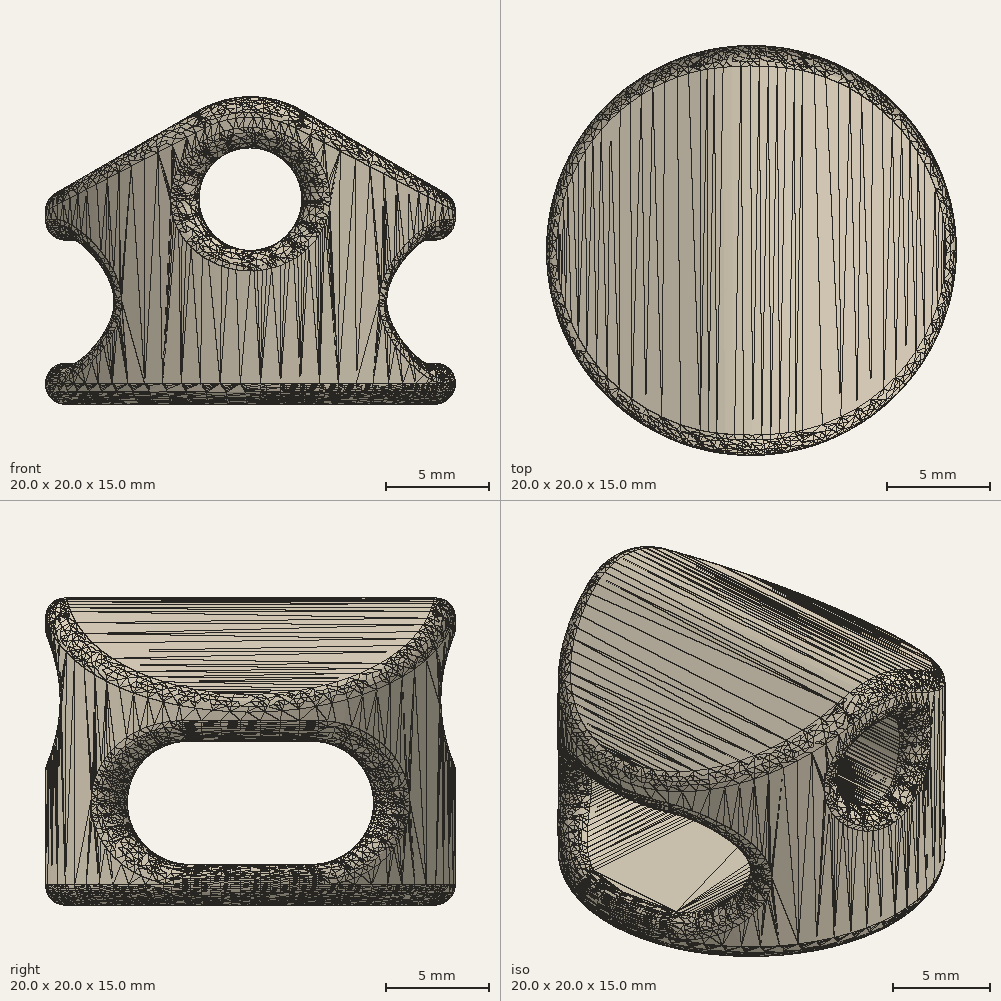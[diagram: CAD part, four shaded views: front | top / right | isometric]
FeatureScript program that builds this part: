
annotation { "Feature Type Name" : "Feature", "Feature Type Description" : "" }
export const myFeature = defineFeature(function(context is Context, id is Id, definition is map)
    precondition{}
    {
        {
            var Q0;
            Q0=qCreatedBy(makeId("Top.planeOp"),FACE);
            var sketch = newSketch(context, id + "F0", { "sketchPlane" : qUnion([Q0])});
            skCircle(sketch, "E0", {"center": v(0, 0) * mm, "radius": 10 * mm});
            skSolve(sketch);
        }
        {
            var Q0;
            Q0 = qSketchRegion(id + "F0", true);
            extrude(context, id + "F1", {"entities" : qUnion([Q0]), "depth" : 10 * mm, "offsetDistance" : 25 * mm, "hasSecondDirection" : true, "secondDirectionOppositeDirection" : true, "secondDirectionDepth" : 5 * mm});
        }
        {
            var Q0;
            Q0=qCreatedBy(makeId("Right.planeOp"),FACE);
            var sketch = newSketch(context, id + "F2", { "sketchPlane" : qUnion([Q0])});
            skLineSegment(sketch, "E1", {"start": v(-3, 0) * mm, "end": v(3, 0) * mm});
            skPoint(sketch, "E2", {"position": v(0, 0) * mm});
            skArc(sketch, "E3.0.startCap", {"start": v(-3, -3) * mm, "mid": v(-6, 0) * mm, "end": v(-3, 3) * mm});
            skArc(sketch, "E3.0.endCap", {"start": v(3, 3) * mm, "mid": v(6, 0) * mm, "end": v(3, -3) * mm});
            skLineSegment(sketch, "E3.0.left", {"start": v(-3, 3) * mm, "end": v(3, 3) * mm});
            skLineSegment(sketch, "E3.0.right", {"start": v(-3, -3) * mm, "end": v(3, -3) * mm});
            skSolve(sketch);
        }
        {
            var Q0;
            Q0 = qSketchRegion(id + "F2", true);
            extrude(context, id + "F3", {"entities" : qUnion([Q0]), "operationType" : NewBodyOperationType.REMOVE, "oppositeDirection" : true, "depth" : 25 * mm, "offsetDistance" : 25 * mm, "hasSecondDirection" : true, "secondDirectionOppositeDirection" : false, "secondDirectionDepth" : 25 * mm});
        }
        {
            var Q0;
            Q0=qCreatedBy(makeId("Front.planeOp"),FACE);
            var sketch = newSketch(context, id + "F4", { "sketchPlane" : qUnion([Q0])});
            skCircle(sketch, "E4", {"center": v(0, 5) * mm, "radius": 2.5 * mm});
            skLineSegment(sketch, "E5.0", {"start": v(-10, 10) * mm, "end": v(10, 10) * mm, "construction": true});
            skLineSegment(sketch, "E6", {"start": v(12.58, 5) * mm, "end": v(-14.82, 5) * mm, "construction": true});
            skPoint(sketch, "E7", {"position": v(-10, 5) * mm});
            skPoint(sketch, "E8", {"position": v(10, 5) * mm});
            skLineSegment(sketch, "E9", {"start": v(10, 5) * mm, "end": v(2.5, 9.33) * mm});
            skLineSegment(sketch, "E10", {"start": v(-10, 5) * mm, "end": v(-2.5, 9.33) * mm});
            skLineSegment(sketch, "E11", {"start": v(-10, 5) * mm, "end": v(-12.41, 5) * mm});
            skLineSegment(sketch, "E12", {"start": v(-12.41, 5) * mm, "end": v(-12.41, 13.56) * mm});
            skLineSegment(sketch, "E13", {"start": v(-12.41, 13.56) * mm, "end": v(12, 13.56) * mm});
            skLineSegment(sketch, "E14", {"start": v(12, 13.56) * mm, "end": v(12, 5) * mm});
            skLineSegment(sketch, "E15", {"start": v(12, 5) * mm, "end": v(10, 5) * mm});
            skLineSegment(sketch, "E16", {"start": v(-2.5, 9.33) * mm, "end": v(-2.5, 9.33) * mm});
            skArc(sketch, "E17", {"start": v(2.5, 9.33) * mm, "mid": v(0, 10) * mm, "end": v(-2.5, 9.33) * mm});
            skArc(sketch, "E18", {"start": v(-2.5, 9.33) * mm, "mid": v(0, 0) * mm, "end": v(2.5, 9.33) * mm, "construction": true});
            skSolve(sketch);
        }
        {
            var Q0;
            Q0 = qSketchRegion(id + "F4", true);
            extrude(context, id + "F5", {"entities" : qUnion([Q0]), "operationType" : NewBodyOperationType.REMOVE, "oppositeDirection" : true, "depth" : 25 * mm, "offsetDistance" : 25 * mm, "hasSecondDirection" : true, "secondDirectionOppositeDirection" : false, "secondDirectionDepth" : 25 * mm});
        }
        {
            var Q0;
            Q0=makeQuery(id+"F1.opExtrude","SWEPT_FACE",FACE,{"disambiguationData":[OSD([sQuery(id+"F0.wireOp",EDGE,"E0")])]});
            fillet(context, id + "F6", {"entities" : qUnion([Q0]), "radius" : 1 * mm, "tangentPropagation" : true, "allowEdgeOverflow" : false});
        }
    });
